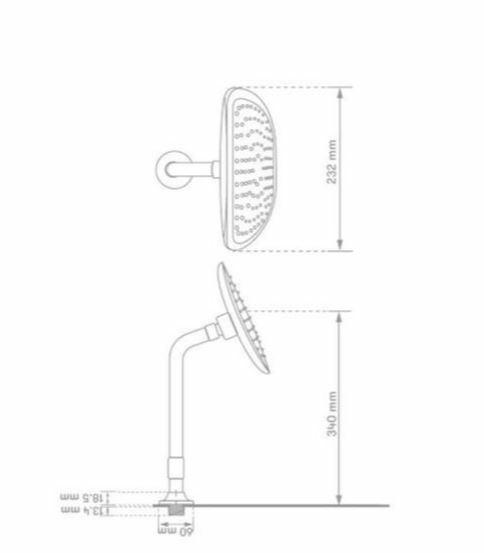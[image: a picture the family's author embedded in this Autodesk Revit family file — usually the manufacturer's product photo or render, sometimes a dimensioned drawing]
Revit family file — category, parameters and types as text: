
# Revit family: 01-1822-11 MEZCLADOR DUCHA 8” CON SALIDA TEDESCA
name_source: partatom
category: Plumbing Fixtures
revit_build: Autodesk Revit 2018 (Build: 20170223_1515(x64)
units: mm (PartAtom-declared; Revit-internal decimal feet)

## family parameters
Cut with Voids When Loaded = No
Host = Face
OmniClass Number = 23.31.11.00
Part Type = Normal
Room Calculation Point = No
Round Connector Dimension = Use Diameter
Shared = No

## types (1)
- 01-1822-11
    Altura - Salida tina = 120 mm
    Ancho escudo = 60 mm  [stored 0.19685 ft]
    CW Connection = Yes
    Default Elevation = 0 mm  [stored 0 ft]
    Description = Mezclador ducha
    Distancia entre griferias = 203.2 mm  [stored 0.666667 ft]
    HW Connection = Yes
    Link Ficha Tecnica = No encontrada en internet
    Manija = 80 mm  [stored 0.262467 ft]
    Manufacturer = Gricol
    Model = 01-1822-11
    Plastico ABS Cromado = Plastico - ABS Cromado
    Product Name = MEZCLADOR DUCHA 8” CON SALIDA TEDESCA
    Type Image = LOGO-01.jpg
    URL = https://www.gricol.com
    Vent Connection = No
    Waste Connection = No

note: [stored X ft] marks values corroborated as IEEE doubles in the binary element streams (Revit-internal decimal feet)

## geometry (parser evidence)
native form markers: Blend x2, Sweep x21
no freeform markers — native parametric forms only
